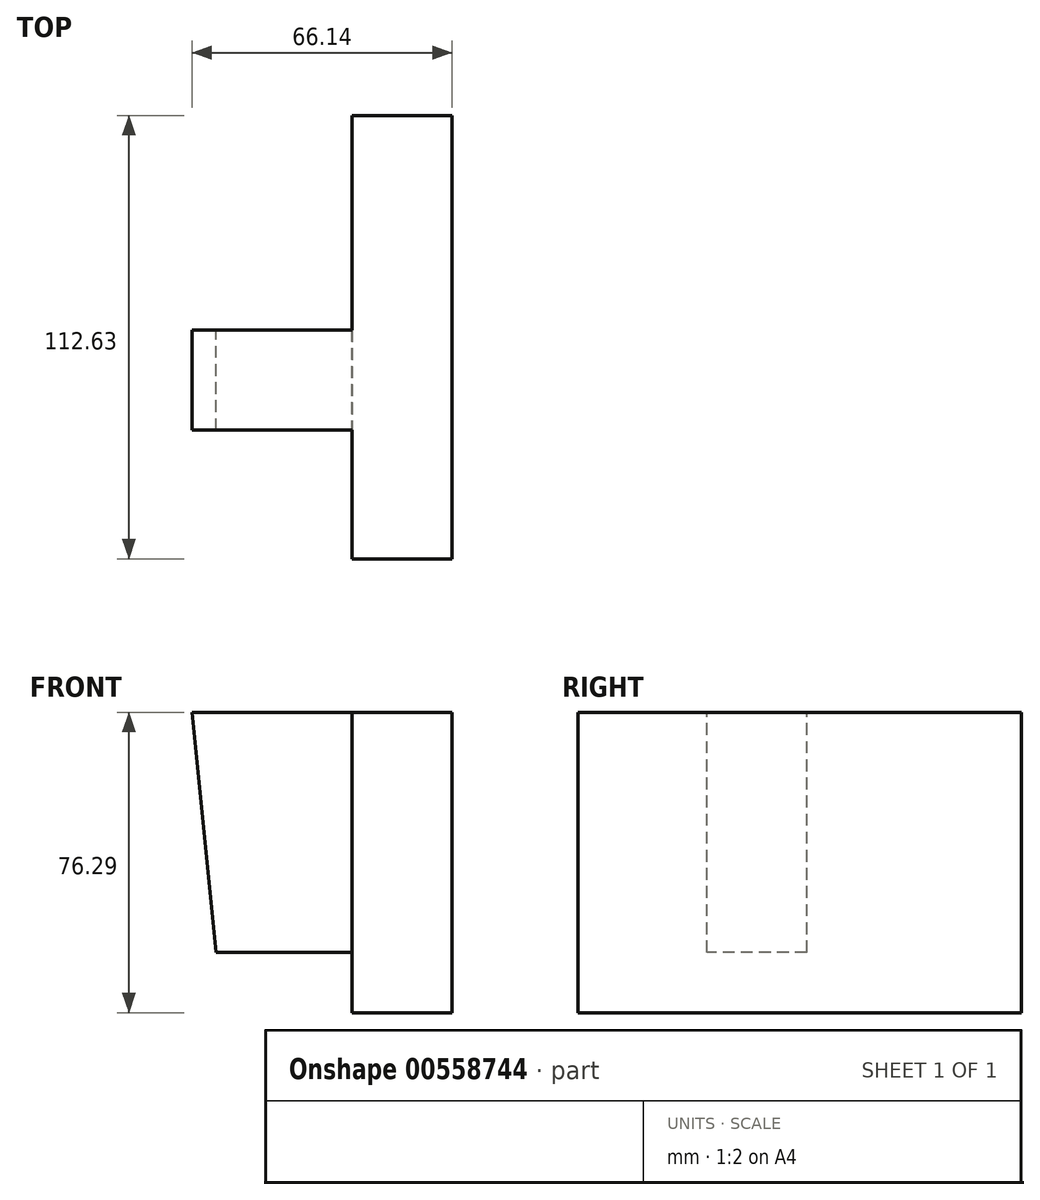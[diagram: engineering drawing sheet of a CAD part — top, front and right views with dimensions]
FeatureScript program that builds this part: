
annotation { "Feature Type Name" : "Feature", "Feature Type Description" : "" }
export const myFeature = defineFeature(function(context is Context, id is Id, definition is map)
    precondition{}
    {
        {
            var Q0;
            Q0=qCreatedBy(makeId("Front.planeOp"),FACE);
            var sketch = newSketch(context, id + "F0", { "sketchPlane" : qUnion([Q0])});
            skLineSegment(sketch, "E0", {"start": v(-40.74, 45.93) * mm, "end": v(25.17, 45.93) * mm});
            skLineSegment(sketch, "E1", {"start": v(25.17, 45.93) * mm, "end": v(25.17, -15) * mm});
            skLineSegment(sketch, "E2", {"start": v(25.17, -15) * mm, "end": v(-34.64, -15) * mm});
            skLineSegment(sketch, "E3", {"start": v(-34.64, -15) * mm, "end": v(-40.74, 45.93) * mm});
            skSolve(sketch);
        }
        {
            var Q0;
            Q0=makeQuery(id+"F0.imprint","IMPRINT",FACE,{"disambiguationData":[TD([[makeQuery(id+"F0.imprint","IMPRINT",EDGE,{"derivedFrom":sQuery(id+"F0.wireOp",EDGE,"E0")}),-1.0]])]});
            extrude(context, id + "F1", {"entities" : qUnion([Q0]), "depth" : 25.4 * mm, "offsetDistance" : 25.4 * mm});
        }
        {
            var Q0;
            Q0=qCreatedBy(makeId("Right.planeOp"),FACE);
            var sketch = newSketch(context, id + "F2", { "sketchPlane" : qUnion([Q0])});
            skLineSegment(sketch, "E4.bottom", {"start": v(-58.12, 45.93) * mm, "end": v(54.5, 45.93) * mm});
            skLineSegment(sketch, "E4.top", {"start": v(-58.12, -30.36) * mm, "end": v(54.5, -30.36) * mm});
            skLineSegment(sketch, "E4.left", {"start": v(-58.12, 45.93) * mm, "end": v(-58.12, -30.36) * mm});
            skLineSegment(sketch, "E4.right", {"start": v(54.5, 45.93) * mm, "end": v(54.5, -30.36) * mm});
            skSolve(sketch);
        }
        {
            var Q0;
            Q0 = qSketchRegion(id + "F2", true);
            extrude(context, id + "F3", {"entities" : qUnion([Q0]), "operationType" : NewBodyOperationType.ADD, "depth" : 25.4 * mm, "offsetDistance" : 25.4 * mm});
        }
    });
